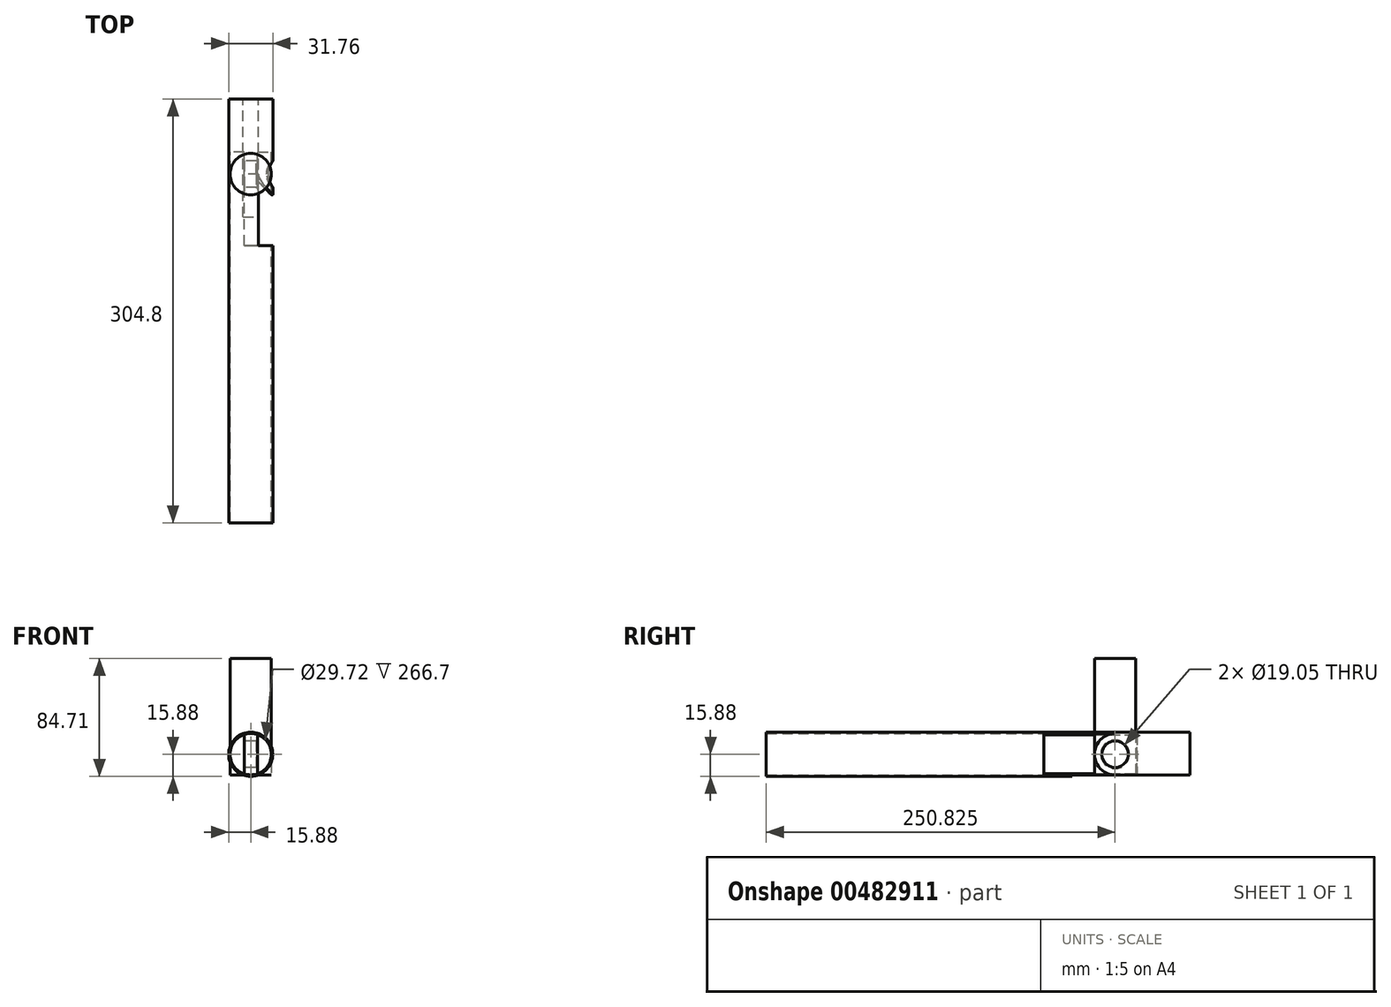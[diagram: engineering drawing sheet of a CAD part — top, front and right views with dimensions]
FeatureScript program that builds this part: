
annotation { "Feature Type Name" : "Feature", "Feature Type Description" : "" }
export const myFeature = defineFeature(function(context is Context, id is Id, definition is map)
    precondition{}
    {
        {
            var Q0;
            Q0=qCreatedBy(makeId("Front.planeOp"),FACE);
            var sketch = newSketch(context, id + "F0", { "sketchPlane" : qUnion([Q0])});
            skCircle(sketch, "E0", {"center": v(0, 0) * mm, "radius": 15.88 * mm});
            skCircle(sketch, "E1", {"center": v(0, 0) * mm, "radius": 14.86 * mm});
            skSolve(sketch);
        }
        {
            var Q0;
            Q0 = qSketchRegion(id + "F0", true);
            extrude(context, id + "F1", {"entities" : qUnion([Q0]), "depth" : 304.8 * mm});
        }
        {
            var Q0;
            Q0=qCreatedBy(makeId("Front.planeOp"),FACE);
            var sketch = newSketch(context, id + "F2", { "sketchPlane" : qUnion([Q0])});
            skCircle(sketch, "E2", {"center": v(0, 0) * mm, "radius": 14.86 * mm});
            skSolve(sketch);
        }
        {
            var Q0;
            Q0 = qSketchRegion(id + "F2", true);
            extrude(context, id + "F3", {"entities" : qUnion([Q0]), "depth" : 38.1 * mm});
        }
        {
            var Q0;
            Q0=makeQuery(id+"F3.opExtrude","CAP_FACE",FACE,{"disambiguationData":[OSD([sQuery(id+"F2.wireOp",EDGE,"E2")])],"isStart":false});
            var sketch = newSketch(context, id + "F4", { "sketchPlane" : qUnion([Q0])});
            skLineSegment(sketch, "E3", {"start": v(-4.75, 14.08) * mm, "end": v(-4.75, -14.08) * mm});
            skLineSegment(sketch, "E4", {"start": v(4.75, 14.08) * mm, "end": v(4.75, -14.08) * mm});
            skArc(sketch, "E5", {"start": v(-4.75, -14.08) * mm, "mid": v(0, -14.86) * mm, "end": v(4.75, -14.08) * mm});
            skArc(sketch, "E6.trimOffspring", {"start": v(4.75, 14.08) * mm, "mid": v(0, 14.86) * mm, "end": v(-4.75, 14.08) * mm});
            skSolve(sketch);
        }
        {
            var Q0;
            Q0 = qSketchRegion(id + "F4", true);
            extrude(context, id + "F5", {"entities" : qUnion([Q0]), "operationType" : NewBodyOperationType.ADD, "depth" : 31.75 * mm});
        }
        {
            var Q0;
            Q0=makeQuery(id+"F5.opExtrude","SWEPT_FACE",FACE,{"disambiguationData":[OSD([sQuery(id+"F4.wireOp",EDGE,"E3")])]});
            var sketch = newSketch(context, id + "F6", { "sketchPlane" : qUnion([Q0])});
            skLineSegment(sketch, "E7", {"start": v(53.97, 42.66) * mm, "end": v(53.98, -51.38) * mm});
            skLineSegment(sketch, "E8", {"start": v(-73.16, 0) * mm, "end": v(128, 0) * mm});
            skCircle(sketch, "E9", {"center": v(53.97, 0) * mm, "radius": 9.53 * mm});
            skSolve(sketch);
        }
        {
            var Q0;
            Q0 = qSketchRegion(id + "F6", true);
            extrude(context, id + "F7", {"entities" : qUnion([Q0]), "operationType" : NewBodyOperationType.REMOVE, "oppositeDirection" : true, "depth" : 25.4 * mm});
        }
        {
            var Q0;
            Q0=makeQuery(id+"F7.boolean.opBoolean","COPY",EDGE,{"derivedFrom":makeQuery(id+"F7.opExtrude","CAP_EDGE",EDGE,{"disambiguationData":[OSD([sQuery(id+"F6.wireOp",EDGE,"E9")])],"isStart":true})});
            var Q1;
            Q1=makeQuery(id+"F7.boolean.opBoolean","INTERSECT",EDGE,{"derivedFrom":[makeQuery(id+"F5.opExtrude","SWEPT_FACE",FACE,{"disambiguationData":[OSD([sQuery(id+"F4.wireOp",EDGE,"E4")])]}),makeQuery(id+"F7.opExtrude","SWEPT_FACE",FACE,{"disambiguationData":[OSD([sQuery(id+"F6.wireOp",EDGE,"E9")])]})]});
            chamfer(context, id + "F8", {"entities" : qUnion([Q0, Q1]), "width" : 0.76 * mm, "tangentPropagation" : true});
        }
        {
            var Q0;
            Q0=makeQuery(id+"F5.opExtrude","SWEPT_EDGE",EDGE,{"disambiguationData":[OSD([sQuery(id+"F2.wireOp",EDGE,"E2"),sQuery(id+"F4.wireOp",EDGE,"E4"),sQuery(id+"F4.wireOp",EDGE,"E6.trimOffspring")])]});
            var Q1;
            Q1=makeQuery(id+"F5.opExtrude","CAP_EDGE",EDGE,{"disambiguationData":[OSD([sQuery(id+"F4.wireOp",EDGE,"E4")])],"isStart":true});
            var Q2;
            {var subQ0=sQuery(id+"F2.wireOp",EDGE,"E2");Q2=makeQuery(id+"F5.boolean.opBoolean","SPLIT",EDGE,{"disambiguationData":[TD([makeQuery(id+"F5.opExtrude","SWEPT_FACE",FACE,{"disambiguationData":[OSD([sQuery(id+"F4.wireOp",EDGE,"E4")])]})])],"derivedFrom":makeQuery(id+"F3.opExtrude","CAP_EDGE",EDGE,{"disambiguationData":[OSD([subQ0])],"isStart":false})});}
            var Q3;
            Q3=makeQuery(id+"F5.opExtrude","CAP_EDGE",EDGE,{"disambiguationData":[OSD([sQuery(id+"F4.wireOp",EDGE,"E4")])],"isStart":false});
            var Q4;
            Q4=makeQuery(id+"F5.opExtrude","CAP_EDGE",EDGE,{"disambiguationData":[OSD([sQuery(id+"F4.wireOp",EDGE,"E6.trimOffspring")])],"isStart":false});
            var Q5;
            Q5=makeQuery(id+"F5.opExtrude","SWEPT_EDGE",EDGE,{"disambiguationData":[OSD([sQuery(id+"F2.wireOp",EDGE,"E2"),sQuery(id+"F4.wireOp",EDGE,"E4"),sQuery(id+"F4.wireOp",EDGE,"E5")])]});
            var Q6;
            Q6=makeQuery(id+"F5.opExtrude","CAP_EDGE",EDGE,{"disambiguationData":[OSD([sQuery(id+"F4.wireOp",EDGE,"E3")])],"isStart":true});
            var Q7;
            {var subQ0=sQuery(id+"F2.wireOp",EDGE,"E2");Q7=makeQuery(id+"F5.boolean.opBoolean","SPLIT",EDGE,{"disambiguationData":[TD([makeQuery(id+"F5.opExtrude","SWEPT_FACE",FACE,{"disambiguationData":[OSD([sQuery(id+"F4.wireOp",EDGE,"E3")])]})])],"derivedFrom":makeQuery(id+"F3.opExtrude","CAP_EDGE",EDGE,{"disambiguationData":[OSD([subQ0])],"isStart":false})});}
            var Q8;
            Q8=makeQuery(id+"F5.opExtrude","SWEPT_EDGE",EDGE,{"disambiguationData":[OSD([sQuery(id+"F2.wireOp",EDGE,"E2"),sQuery(id+"F4.wireOp",EDGE,"E3"),sQuery(id+"F4.wireOp",EDGE,"E5")])]});
            var Q9;
            Q9=makeQuery(id+"F5.opExtrude","SWEPT_EDGE",EDGE,{"disambiguationData":[OSD([sQuery(id+"F2.wireOp",EDGE,"E2"),sQuery(id+"F4.wireOp",EDGE,"E3"),sQuery(id+"F4.wireOp",EDGE,"E6.trimOffspring")])]});
            var Q10;
            Q10=makeQuery(id+"F5.opExtrude","CAP_EDGE",EDGE,{"disambiguationData":[OSD([sQuery(id+"F4.wireOp",EDGE,"E3")])],"isStart":false});
            var Q11;
            Q11=makeQuery(id+"F5.opExtrude","CAP_EDGE",EDGE,{"disambiguationData":[OSD([sQuery(id+"F4.wireOp",EDGE,"E5")])],"isStart":false});
            var Q12;
            Q12=makeQuery(id+"F3.opExtrude","CAP_EDGE",EDGE,{"disambiguationData":[OSD([sQuery(id+"F2.wireOp",EDGE,"E2")])],"isStart":true});
            fillet(context, id + "F9", {"entities" : qUnion([Q0, Q1, Q2, Q3, Q4, Q5, Q6, Q7, Q8, Q9, Q10, Q11, Q12]), "radius" : 0.25 * mm, "tangentPropagation" : true, "allowEdgeOverflow" : false});
        }
        {
            var Q0;
            Q0=makeQuery(id+"F5.opExtrude","SWEPT_FACE",FACE,{"disambiguationData":[OSD([sQuery(id+"F4.wireOp",EDGE,"E3")])]});
            var sketch = newSketch(context, id + "F10", { "sketchPlane" : qUnion([Q0])});
            skLineSegment(sketch, "E10", {"start": v(53.97, 14.86) * mm, "end": v(105.24, 14.86) * mm});
            skLineSegment(sketch, "E11", {"start": v(105.24, 14.86) * mm, "end": v(105.24, -14.86) * mm});
            skLineSegment(sketch, "E12", {"start": v(105.24, -14.86) * mm, "end": v(53.97, -14.86) * mm});
            skArc(sketch, "E13", {"start": v(53.97, -14.86) * mm, "mid": v(68.83, 0) * mm, "end": v(53.97, 14.86) * mm});
            skSolve(sketch);
        }
        {
            var Q0;
            Q0 = qSketchRegion(id + "F10", true);
            extrude(context, id + "F11", {"entities" : qUnion([Q0]), "operationType" : NewBodyOperationType.REMOVE, "oppositeDirection" : true, "depth" : 25.4 * mm});
        }
        {
            var Q0;
            Q0=makeQuery(id+"F11.boolean.opBoolean","COPY",EDGE,{"derivedFrom":makeQuery(id+"F11.opExtrude","CAP_EDGE",EDGE,{"disambiguationData":[OSD([sQuery(id+"F10.wireOp",EDGE,"E13")])],"isStart":true})});
            var Q1;
            Q1=makeQuery(id+"F11.boolean.opBoolean","INTERSECT",EDGE,{"derivedFrom":[makeQuery(id+"F5.opExtrude","SWEPT_FACE",FACE,{"disambiguationData":[OSD([sQuery(id+"F4.wireOp",EDGE,"E4")])]}),makeQuery(id+"F11.opExtrude","SWEPT_FACE",FACE,{"disambiguationData":[OSD([sQuery(id+"F10.wireOp",EDGE,"E13")])]})]});
            fillet(context, id + "F12", {"entities" : qUnion([Q0, Q1]), "radius" : 0.25 * mm, "tangentPropagation" : true, "allowEdgeOverflow" : false});
        }
        {
            var Q0;
            Q0=qCreatedBy(makeId("Top.planeOp"),FACE);
            var sketch = newSketch(context, id + "F13", { "sketchPlane" : qUnion([Q0])});
            skLineSegment(sketch, "E14", {"start": v(-49.18, -53.98) * mm, "end": v(80.67, -53.98) * mm});
            skLineSegment(sketch, "E15", {"start": v(0, 65.44) * mm, "end": v(0, -75.07) * mm});
            skCircle(sketch, "E16", {"center": v(0, -53.98) * mm, "radius": 14.86 * mm});
            skSolve(sketch);
        }
        {
            var Q0;
            Q0 = qSketchRegion(id + "F13", true);
            extrude(context, id + "F14", {"entities" : qUnion([Q0]), "endBound" : BoundingType.SYMMETRIC, "depth" : 137.67 * mm});
        }
        {
            var Q0;
            Q0=qCreatedBy(makeId("Right.planeOp"),FACE);
            var sketch = newSketch(context, id + "F15", { "sketchPlane" : qUnion([Q0])});
            skLineSegment(sketch, "E17", {"start": v(1.35, -14.88) * mm, "end": v(-84.87, -14.88) * mm});
            skLineSegment(sketch, "E18", {"start": v(-84.87, -14.88) * mm, "end": v(-84.87, -78.38) * mm});
            skLineSegment(sketch, "E19", {"start": v(-84.87, -78.38) * mm, "end": v(1.35, -78.38) * mm});
            skLineSegment(sketch, "E20", {"start": v(1.35, -78.38) * mm, "end": v(1.35, -14.88) * mm});
            skSolve(sketch);
        }
        {
            var Q0;
            Q0 = qSketchRegion(id + "F15", true);
            extrude(context, id + "F16", {"entities" : qUnion([Q0]), "operationType" : NewBodyOperationType.REMOVE, "endBound" : BoundingType.SYMMETRIC, "oppositeDirection" : true, "depth" : 101.6 * mm});
        }
    });
